# Revit family: 98462C6A SMART COMMAND ETAP WALL MOUNTED BASIN - KIT
name_source: partatom
category: Plumbing Fixtures
revit_build: Autodesk Revit 2015 (Build: 20140606_1530(x64)
units: mm (PartAtom-declared; Revit-internal decimal feet)

## types (1)
- SMART COMMAND ETAP WALL MOUNTED BASIN - KIT
    Assembly Code = C1030220
    CW Connection = No
    Default Elevation = 900 mm  [stored 2.95276 ft]
    Description = SMART COMMAND ETAP WALL MOUNTED BASIN - KIT
    HW Connection = Yes
    Manufacturer = GWA Bathrooms & Kitchens
    Material_Elect = GWA-Plastic-Black
    Material_Sensor = GWA-Metal-Black
    Material_Spout = GWA_Metal-Chrome
    Model = 98462C6A
    Type Comments = 98462C6A Consists of 2x Components 98450  &  98451C6A
    URL = https://www.caroma.com.au
    Vent Connection = No
    Waste Connection = No

note: [stored X ft] marks values corroborated as IEEE doubles in the binary element streams (Revit-internal decimal feet)

## geometry (parser evidence)
native form markers: Sweep x2
no freeform markers — native parametric forms only
